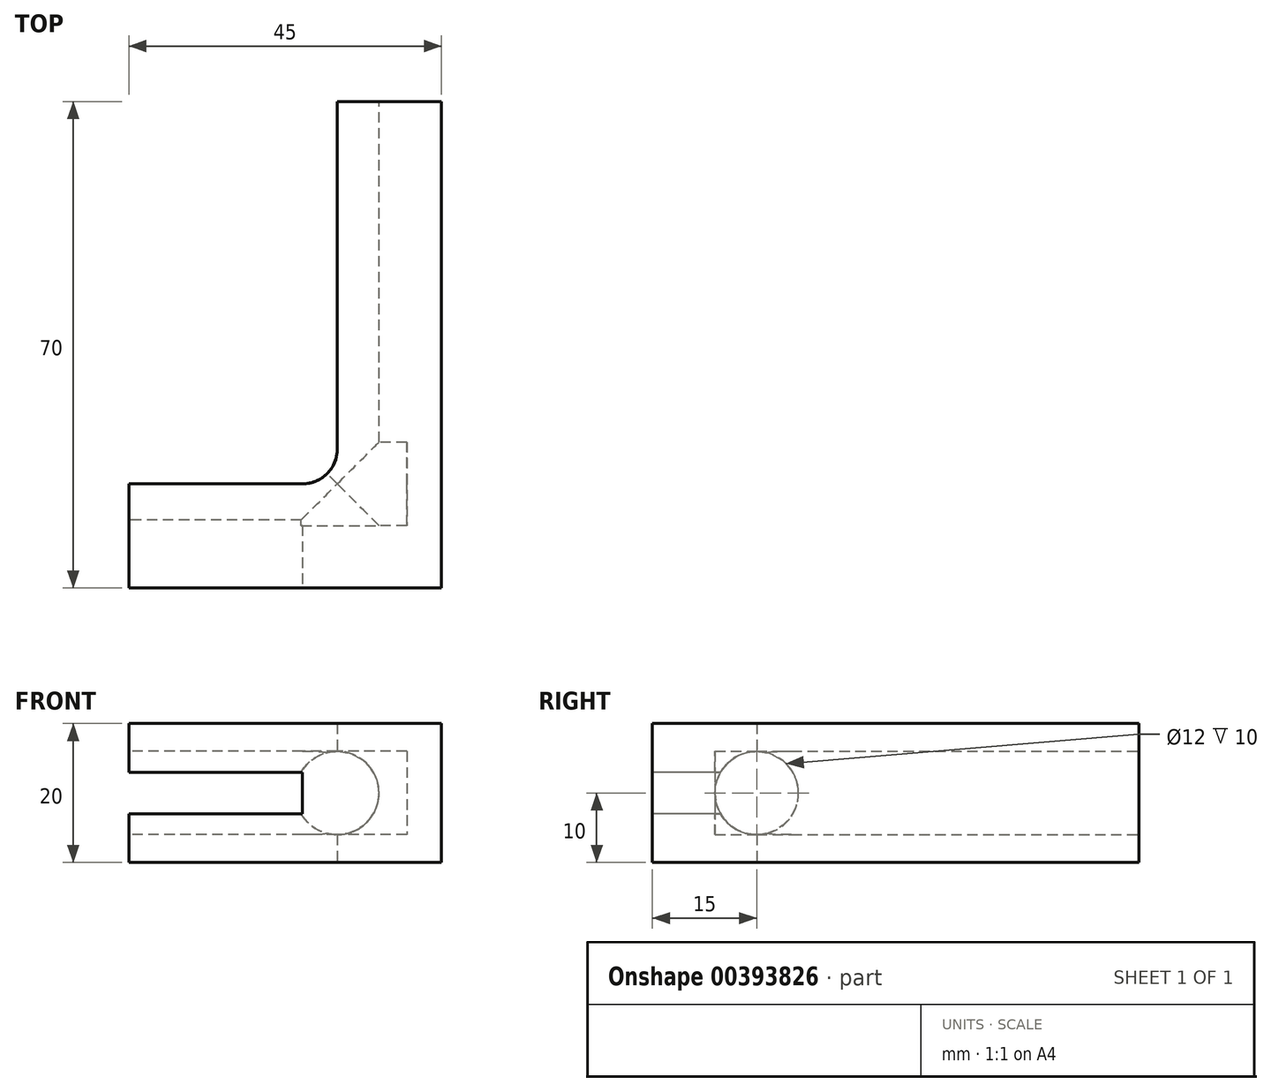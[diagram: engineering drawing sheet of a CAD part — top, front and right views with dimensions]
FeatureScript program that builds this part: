
annotation { "Feature Type Name" : "Feature", "Feature Type Description" : "" }
export const myFeature = defineFeature(function(context is Context, id is Id, definition is map)
    precondition{}
    {
        {
            var Q0;
            Q0=qCreatedBy(makeId("Top.planeOp"),FACE);
            var sketch = newSketch(context, id + "F0", { "sketchPlane" : qUnion([Q0])});
            skLineSegment(sketch, "E0.bottom", {"start": v(7.5, 35) * mm, "end": v(22.5, 35) * mm});
            skLineSegment(sketch, "E0.top", {"start": v(-22.5, -35) * mm, "end": v(22.5, -35) * mm});
            skLineSegment(sketch, "E0.left", {"start": v(-22.5, -20) * mm, "end": v(-22.5, -35) * mm});
            skLineSegment(sketch, "E0.right", {"start": v(22.5, 35) * mm, "end": v(22.5, -35) * mm});
            skArc(sketch, "E1", {"start": v(2.5, -20) * mm, "mid": v(6.04, -18.54) * mm, "end": v(7.5, -15) * mm});
            skLineSegment(sketch, "E2", {"start": v(-22.5, -20) * mm, "end": v(2.5, -20) * mm});
            skLineSegment(sketch, "E3", {"start": v(7.5, -15) * mm, "end": v(7.5, 35) * mm});
            skSolve(sketch);
        }
        {
            var Q0;
            Q0 = qSketchRegion(id + "F0", true);
            extrude(context, id + "F1", {"entities" : qUnion([Q0]), "depth" : 20 * mm});
        }
        {
            var Q0;
            Q0=makeQuery(id+"F1.opExtrude","SWEPT_FACE",FACE,{"disambiguationData":[OSD([sQuery(id+"F0.wireOp",EDGE,"E0.left")])]});
            var sketch = newSketch(context, id + "F2", { "sketchPlane" : qUnion([Q0])});
            skCircle(sketch, "E4", {"center": v(20, 10) * mm, "radius": 6 * mm});
            skSolve(sketch);
        }
        {
            var Q0;
            Q0 = qSketchRegion(id + "F2", true);
            extrude(context, id + "F3", {"entities" : qUnion([Q0]), "operationType" : NewBodyOperationType.REMOVE, "oppositeDirection" : true, "depth" : 40 * mm});
        }
        {
            var Q0;
            Q0=makeQuery(id+"F1.opExtrude","SWEPT_FACE",FACE,{"disambiguationData":[OSD([sQuery(id+"F0.wireOp",EDGE,"E0.bottom")])]});
            var sketch = newSketch(context, id + "F4", { "sketchPlane" : qUnion([Q0])});
            skCircle(sketch, "E5", {"center": v(-7.5, 10) * mm, "radius": 6 * mm});
            skSolve(sketch);
        }
        {
            var Q0;
            Q0 = qSketchRegion(id + "F4", true);
            extrude(context, id + "F5", {"entities" : qUnion([Q0]), "operationType" : NewBodyOperationType.REMOVE, "oppositeDirection" : true, "depth" : 61 * mm});
        }
        {
            var Q0;
            Q0=makeQuery(id+"F1.opExtrude","SWEPT_FACE",FACE,{"disambiguationData":[OSD([sQuery(id+"F0.wireOp",EDGE,"E0.top")])]});
            var sketch = newSketch(context, id + "F6", { "sketchPlane" : qUnion([Q0])});
            skLineSegment(sketch, "E6.bottom", {"start": v(-22.5, 7) * mm, "end": v(2.5, 7) * mm});
            skLineSegment(sketch, "E6.top", {"start": v(-22.5, 13) * mm, "end": v(2.5, 13) * mm});
            skLineSegment(sketch, "E6.left", {"start": v(-22.5, 7) * mm, "end": v(-22.5, 13) * mm});
            skLineSegment(sketch, "E6.right", {"start": v(2.5, 7) * mm, "end": v(2.5, 13) * mm});
            skSolve(sketch);
        }
        {
            var Q0;
            Q0=makeQuery(id+"F6.imprint","IMPRINT",FACE,{"disambiguationData":[TD([[makeQuery(id+"F6.imprint","IMPRINT",EDGE,{"derivedFrom":sQuery(id+"F6.wireOp",EDGE,"E6.bottom")}),1.0]])]});
            extrude(context, id + "F7", {"entities" : qUnion([Q0]), "operationType" : NewBodyOperationType.REMOVE, "oppositeDirection" : true, "depth" : 25 * mm});
        }
    });
